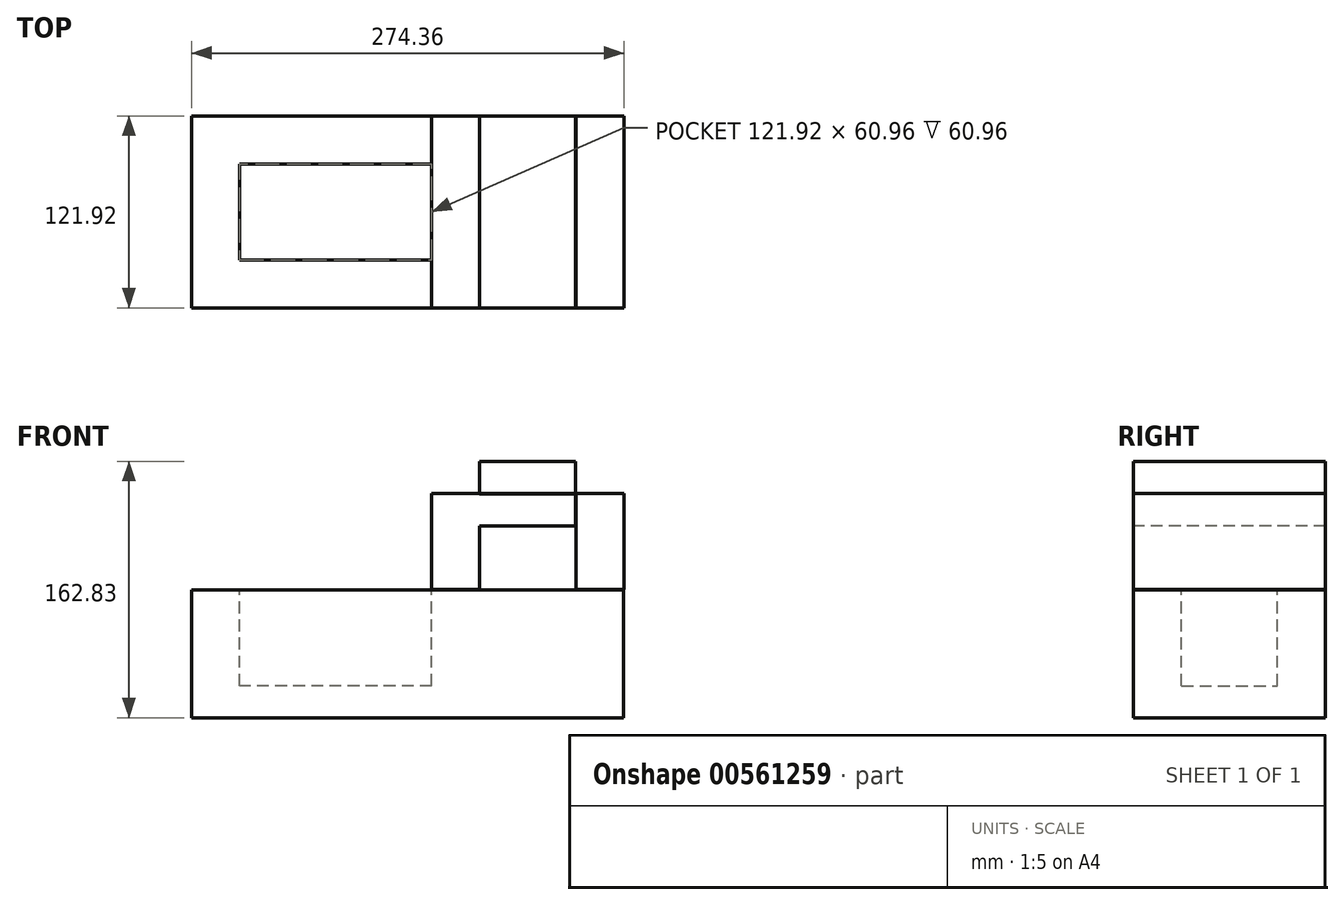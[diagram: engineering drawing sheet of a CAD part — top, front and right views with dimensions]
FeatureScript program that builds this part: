
annotation { "Feature Type Name" : "Feature", "Feature Type Description" : "" }
export const myFeature = defineFeature(function(context is Context, id is Id, definition is map)
    precondition{}
    {
        {
            var Q0;
            Q0=qCreatedBy(makeId("Front.planeOp"),FACE);
            var sketch = newSketch(context, id + "F0", { "sketchPlane" : qUnion([Q0])});
            skLineSegment(sketch, "E0", {"start": v(0, 0) * mm, "end": v(121.92, 0) * mm});
            skLineSegment(sketch, "E1", {"start": v(121.92, 0) * mm, "end": v(121.92, 81.28) * mm});
            skLineSegment(sketch, "E2", {"start": v(121.92, 81.28) * mm, "end": v(0, 81.28) * mm});
            skLineSegment(sketch, "E3", {"start": v(0, 81.28) * mm, "end": v(0, 0) * mm});
            skSolve(sketch);
        }
        {
            var Q0;
            Q0 = qSketchRegion(id + "F0", true);
            extrude(context, id + "F1", {"entities" : qUnion([Q0]), "depth" : 121.92 * mm, "offsetDistance" : 25.4 * mm});
        }
        {
            var Q0;
            Q0=qCreatedBy(makeId("Front.planeOp"),FACE);
            var sketch = newSketch(context, id + "F2", { "sketchPlane" : qUnion([Q0])});
            skLineSegment(sketch, "E4", {"start": v(0, 81.36) * mm, "end": v(0, 142.32) * mm});
            skLineSegment(sketch, "E5", {"start": v(0, 142.32) * mm, "end": v(30.48, 142.32) * mm});
            skLineSegment(sketch, "E6", {"start": v(30.48, 142.32) * mm, "end": v(30.48, 81.36) * mm});
            skLineSegment(sketch, "E7", {"start": v(30.48, 81.36) * mm, "end": v(0, 81.36) * mm});
            skSolve(sketch);
        }
        {
            var Q0;
            Q0 = qSketchRegion(id + "F2", true);
            extrude(context, id + "F3", {"entities" : qUnion([Q0]), "depth" : 121.92 * mm, "offsetDistance" : 25.4 * mm});
        }
        {
            var Q0;
            Q0=qCreatedBy(makeId("Front.planeOp"),FACE);
            var sketch = newSketch(context, id + "F4", { "sketchPlane" : qUnion([Q0])});
            skLineSegment(sketch, "E8", {"start": v(121.96, 81.38) * mm, "end": v(121.96, 142.34) * mm});
            skLineSegment(sketch, "E9", {"start": v(121.96, 142.34) * mm, "end": v(91.48, 142.34) * mm});
            skLineSegment(sketch, "E10", {"start": v(91.48, 142.34) * mm, "end": v(91.48, 81.38) * mm});
            skLineSegment(sketch, "E11", {"start": v(91.48, 81.38) * mm, "end": v(121.96, 81.38) * mm});
            skSolve(sketch);
        }
        {
            var Q0;
            Q0=qCreatedBy(makeId("Front.planeOp"),FACE);
            var sketch = newSketch(context, id + "F5", { "sketchPlane" : qUnion([Q0])});
            skLineSegment(sketch, "E12", {"start": v(30.22, 121.89) * mm, "end": v(91.18, 121.89) * mm});
            skLineSegment(sketch, "E13", {"start": v(30.22, 121.89) * mm, "end": v(30.22, 142.2) * mm});
            skLineSegment(sketch, "E14", {"start": v(30.22, 142.2) * mm, "end": v(91.18, 142.2) * mm});
            skLineSegment(sketch, "E15", {"start": v(91.18, 142.2) * mm, "end": v(91.18, 121.89) * mm});
            skSolve(sketch);
        }
        {
            var Q0;
            Q0 = qSketchRegion(id + "F5", true);
            var Q1;
            Q1=makeQuery(id+"F4.imprint","IMPRINT",FACE,{"disambiguationData":[TD([[makeQuery(id+"F4.imprint","IMPRINT",EDGE,{"derivedFrom":sQuery(id+"F4.wireOp",EDGE,"E8")}),1.0]])]});
            extrude(context, id + "F6", {"entities" : qUnion([Q0, Q1]), "operationType" : NewBodyOperationType.ADD, "depth" : 121.92 * mm, "offsetDistance" : 25.4 * mm});
        }
        {
            var Q0;
            Q0=qCreatedBy(makeId("Front.planeOp"),FACE);
            var sketch = newSketch(context, id + "F7", { "sketchPlane" : qUnion([Q0])});
            skLineSegment(sketch, "E16", {"start": v(30.48, 142.51) * mm, "end": v(30.48, 162.83) * mm});
            skLineSegment(sketch, "E17", {"start": v(30.48, 162.83) * mm, "end": v(91.44, 162.83) * mm});
            skLineSegment(sketch, "E18", {"start": v(91.44, 162.83) * mm, "end": v(91.44, 142.51) * mm});
            skLineSegment(sketch, "E19", {"start": v(91.44, 142.51) * mm, "end": v(30.48, 142.51) * mm});
            skSolve(sketch);
        }
        {
            var Q0;
            Q0 = qSketchRegion(id + "F7", true);
            extrude(context, id + "F8", {"entities" : qUnion([Q0]), "depth" : 121.92 * mm, "offsetDistance" : 25.4 * mm});
        }
        {
            var Q0;
            Q0=qCreatedBy(makeId("Front.planeOp"),FACE);
            var sketch = newSketch(context, id + "F9", { "sketchPlane" : qUnion([Q0])});
            skLineSegment(sketch, "E20", {"start": v(0, 0) * mm, "end": v(0, 81.28) * mm});
            skLineSegment(sketch, "E21", {"start": v(0, 81.28) * mm, "end": v(-152.4, 81.28) * mm});
            skLineSegment(sketch, "E22", {"start": v(-152.4, 81.28) * mm, "end": v(-152.4, 0) * mm});
            skLineSegment(sketch, "E23", {"start": v(-152.4, 0) * mm, "end": v(0, 0) * mm});
            skSolve(sketch);
        }
        {
            var Q0;
            Q0 = qSketchRegion(id + "F9", true);
            extrude(context, id + "F10", {"entities" : qUnion([Q0]), "operationType" : NewBodyOperationType.ADD, "depth" : 121.92 * mm, "offsetDistance" : 25.4 * mm});
        }
        {
            var Q0;
            Q0=makeQuery(id+"F10.boolean.opBoolean","MERGE",FACE,{"derivedFrom":[makeQuery(id+"F1.opExtrude","SWEPT_FACE",FACE,{"disambiguationData":[OSD([sQuery(id+"F0.wireOp",EDGE,"E2")])]}),makeQuery(id+"F10.opExtrude","SWEPT_FACE",FACE,{"disambiguationData":[OSD([sQuery(id+"F9.wireOp",EDGE,"E21")])]})]});
            var sketch = newSketch(context, id + "F11", { "sketchPlane" : qUnion([Q0])});
            skLineSegment(sketch, "E24", {"start": v(0, -30.48) * mm, "end": v(-121.92, -30.48) * mm});
            skLineSegment(sketch, "E25", {"start": v(-121.92, -30.48) * mm, "end": v(-121.92, -91.44) * mm});
            skLineSegment(sketch, "E26", {"start": v(-121.92, -91.44) * mm, "end": v(0, -91.44) * mm});
            skLineSegment(sketch, "E27", {"start": v(0, -91.44) * mm, "end": v(0, -30.48) * mm});
            skSolve(sketch);
        }
        {
            var Q0;
            Q0=makeQuery(id+"F11.imprint","IMPRINT",FACE,{"disambiguationData":[TD([[makeQuery(id+"F11.imprint","IMPRINT",EDGE,{"derivedFrom":sQuery(id+"F11.wireOp",EDGE,"E24")}),1.0]])]});
            extrude(context, id + "F12", {"entities" : qUnion([Q0]), "operationType" : NewBodyOperationType.REMOVE, "oppositeDirection" : true, "depth" : 60.96 * mm, "offsetDistance" : 25.4 * mm});
        }
    });
